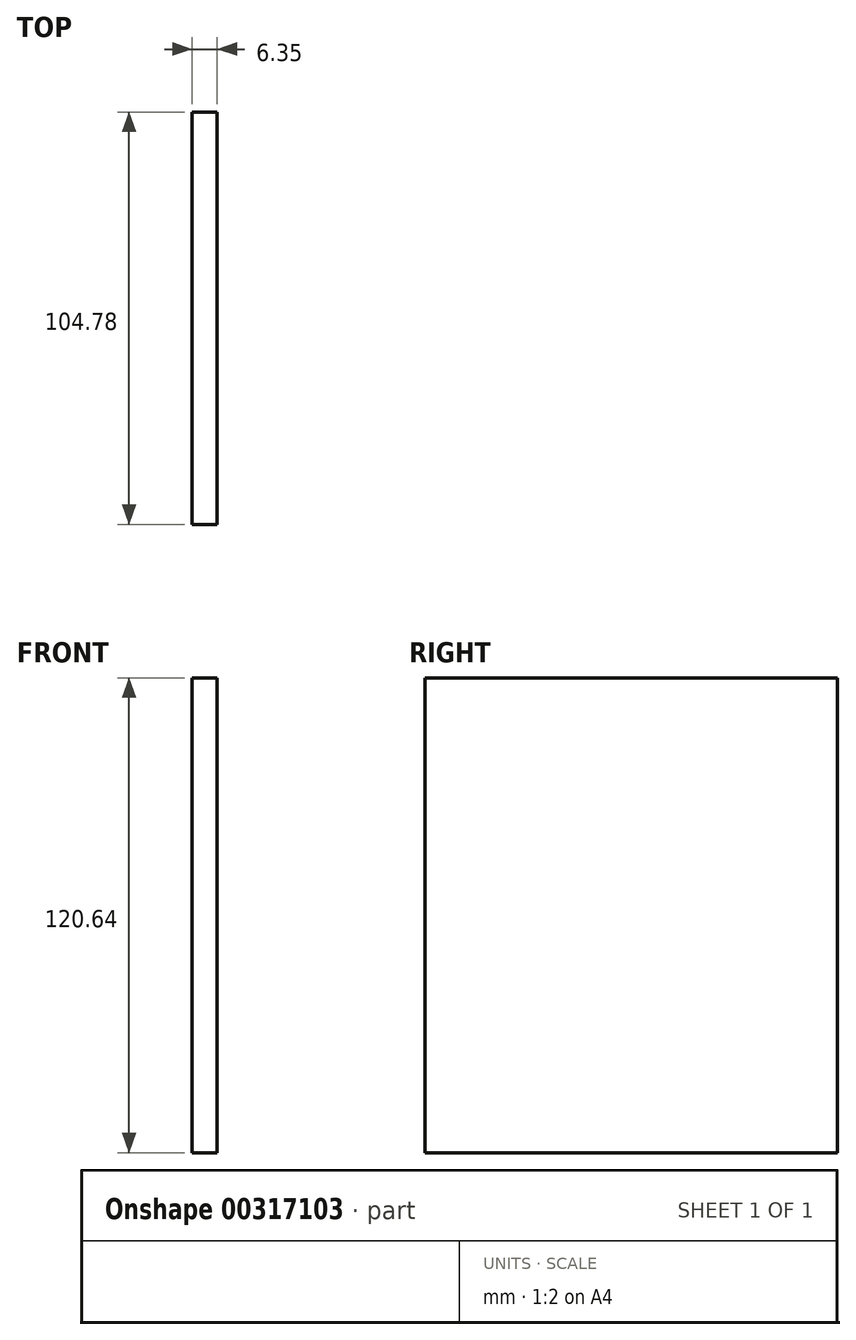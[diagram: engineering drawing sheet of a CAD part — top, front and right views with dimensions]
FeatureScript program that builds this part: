
annotation { "Feature Type Name" : "Feature", "Feature Type Description" : "" }
export const myFeature = defineFeature(function(context is Context, id is Id, definition is map)
    precondition{}
    {
        {
            var Q0;
            Q0=qCreatedBy(makeId("Right.planeOp"),FACE);
            var sketch = newSketch(context, id + "F0", { "sketchPlane" : qUnion([Q0])});
            skLineSegment(sketch, "E0.bottom", {"start": v(52.39, 60.33) * mm, "end": v(-52.39, 60.32) * mm});
            skLineSegment(sketch, "E0.top", {"start": v(52.39, -60.33) * mm, "end": v(-52.39, -60.33) * mm});
            skLineSegment(sketch, "E0.left", {"start": v(52.39, 60.33) * mm, "end": v(52.39, -60.33) * mm});
            skLineSegment(sketch, "E0.right", {"start": v(-52.39, 60.33) * mm, "end": v(-52.39, -60.33) * mm});
            skPoint(sketch, "E0.middle", {"position": v(0, 0) * mm});
            skLineSegment(sketch, "E1.bottom", {"start": v(-52.39, 60.32) * mm, "end": v(-46.04, 60.32) * mm});
            skLineSegment(sketch, "E1.top", {"start": v(-52.39, 63.5) * mm, "end": v(-46.04, 63.5) * mm});
            skLineSegment(sketch, "E1.left", {"start": v(-52.39, 60.33) * mm, "end": v(-52.39, 63.5) * mm});
            skLineSegment(sketch, "E1.right", {"start": v(-46.04, 60.33) * mm, "end": v(-46.04, 63.5) * mm});
            skLineSegment(sketch, "E2.bottom", {"start": v(-52.39, -60.33) * mm, "end": v(-46.04, -60.33) * mm});
            skLineSegment(sketch, "E2.top", {"start": v(-52.39, -63.5) * mm, "end": v(-46.04, -63.5) * mm});
            skLineSegment(sketch, "E2.left", {"start": v(-52.39, -60.33) * mm, "end": v(-52.39, -63.5) * mm});
            skLineSegment(sketch, "E2.right", {"start": v(-46.04, -60.33) * mm, "end": v(-46.04, -63.5) * mm});
            skSolve(sketch);
        }
        {
            var Q0;
            Q0=makeQuery(id+"F0.imprint","IMPRINT",FACE,{"disambiguationData":[TD([[makeQuery(id+"F0.imprint","IMPRINT",EDGE,{"derivedFrom":sQuery(id+"F0.wireOp",EDGE,"E0.bottom")}),1.0]])]});
            var Q1;
            Q1=makeQuery(id+"F0.imprint","IMPRINT",FACE,{"disambiguationData":[TD([[makeQuery(id+"F0.imprint","IMPRINT",EDGE,{"derivedFrom":sQuery(id+"F0.wireOp",EDGE,"E1.bottom")}),1.0]])]});
            var Q2;
            Q2=makeQuery(id+"F0.imprint","IMPRINT",FACE,{"disambiguationData":[TD([[makeQuery(id+"F0.imprint","IMPRINT",EDGE,{"derivedFrom":sQuery(id+"F0.wireOp",EDGE,"E2.bottom")}),-1.0]])]});
            extrude(context, id + "F1", {"entities" : qUnion([Q0, Q1, Q2]), "depth" : 6.35 * mm});
        }
    });
